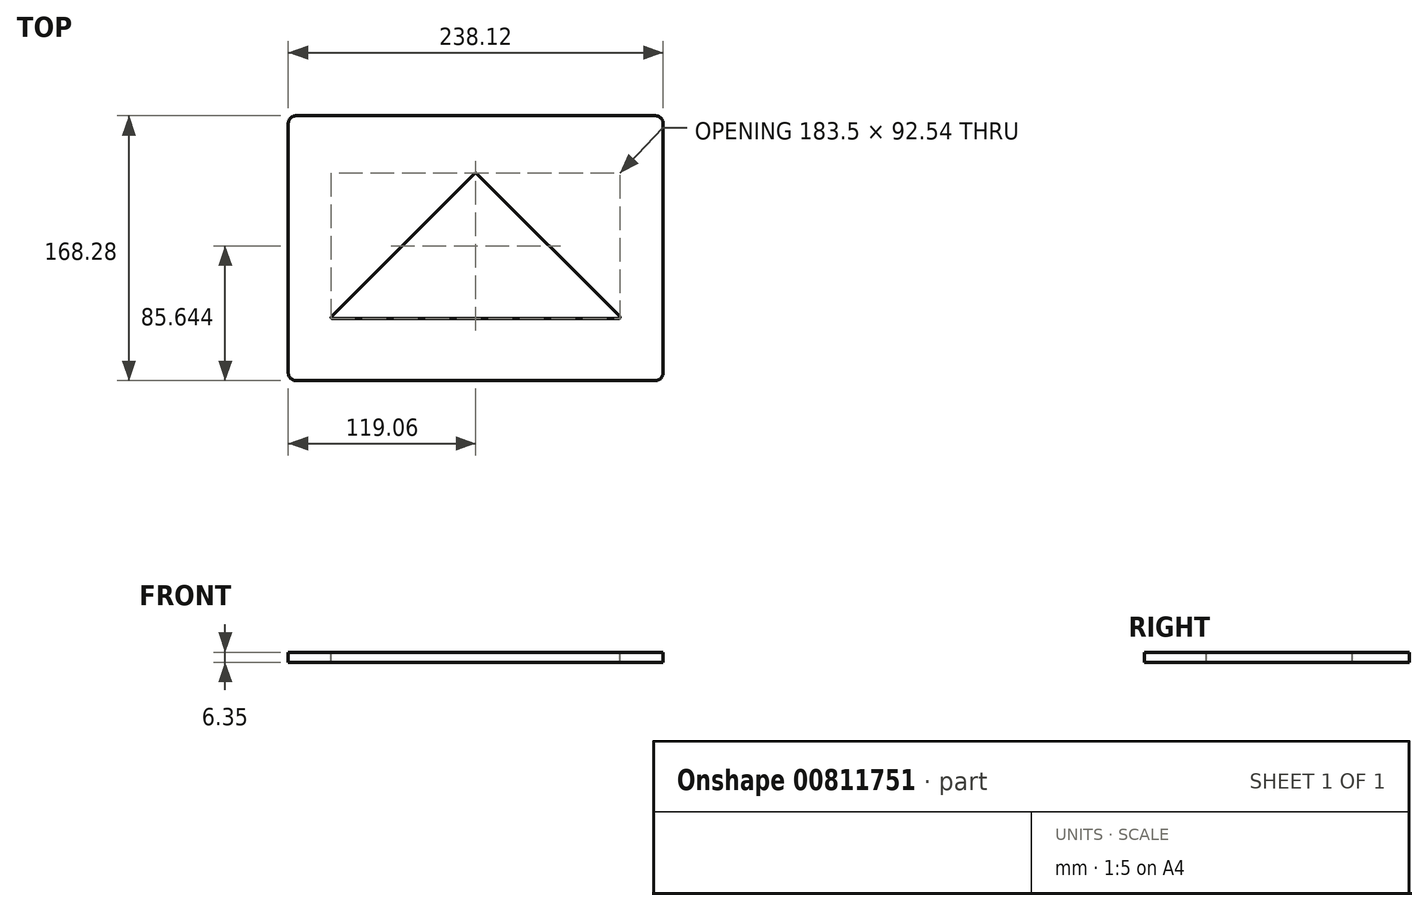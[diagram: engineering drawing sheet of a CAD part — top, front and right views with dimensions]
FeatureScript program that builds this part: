
annotation { "Feature Type Name" : "Feature", "Feature Type Description" : "" }
export const myFeature = defineFeature(function(context is Context, id is Id, definition is map)
    precondition{}
    {
        {
            var Q0;
            Q0=qCreatedBy(makeId("Top.planeOp"),FACE);
            var sketch = newSketch(context, id + "F0", { "sketchPlane" : qUnion([Q0])});
            skLineSegment(sketch, "E0.bottom", {"start": v(-113.98, 84.14) * mm, "end": v(113.98, 84.14) * mm});
            skLineSegment(sketch, "E0.top", {"start": v(-113.98, -84.14) * mm, "end": v(113.98, -84.14) * mm});
            skLineSegment(sketch, "E0.left", {"start": v(-119.06, 79.06) * mm, "end": v(-119.06, -79.06) * mm});
            skLineSegment(sketch, "E0.right", {"start": v(119.06, 79.06) * mm, "end": v(119.06, -79.06) * mm});
            skPoint(sketch, "E0.middle", {"position": v(0, 0) * mm});
            skPoint(sketch, "E1.visualSharp", {"position": v(-119.06, 84.14) * mm});
            skArc(sketch, "E1.filletArc", {"start": v(-113.98, 84.14) * mm, "mid": v(-117.57, 82.65) * mm, "end": v(-119.06, 79.06) * mm});
            skPoint(sketch, "E2.visualSharp", {"position": v(119.06, 84.14) * mm});
            skArc(sketch, "E2.filletArc", {"start": v(119.06, 79.06) * mm, "mid": v(117.57, 82.65) * mm, "end": v(113.98, 84.14) * mm});
            skPoint(sketch, "E3.visualSharp", {"position": v(119.06, -84.14) * mm});
            skArc(sketch, "E3.filletArc", {"start": v(113.98, -84.14) * mm, "mid": v(117.57, -82.65) * mm, "end": v(119.06, -79.06) * mm});
            skPoint(sketch, "E4.visualSharp", {"position": v(-119.06, -84.14) * mm});
            skArc(sketch, "E4.filletArc", {"start": v(-119.06, -79.06) * mm, "mid": v(-117.57, -82.65) * mm, "end": v(-113.98, -84.14) * mm});
            skSolve(sketch);
        }
        {
            var Q0;
            Q0 = qSketchRegion(id + "F0", true);
            extrude(context, id + "F1", {"entities" : qUnion([Q0]), "depth" : 6.35 * mm, "offsetDistance" : 25.4 * mm});
        }
        {
            var Q0;
            Q0=makeQuery(id+"F1.opExtrude","CAP_FACE",FACE,{"disambiguationData":[OSD([sQuery(id+"F0.wireOp",EDGE,"E0.bottom"),sQuery(id+"F0.wireOp",EDGE,"E0.top"),sQuery(id+"F0.wireOp",EDGE,"E0.left"),sQuery(id+"F0.wireOp",EDGE,"E0.right"),sQuery(id+"F0.wireOp",EDGE,"E1.filletArc"),sQuery(id+"F0.wireOp",EDGE,"E2.filletArc"),sQuery(id+"F0.wireOp",EDGE,"E3.filletArc"),sQuery(id+"F0.wireOp",EDGE,"E4.filletArc")])],"isStart":false});
            var sketch = newSketch(context, id + "F2", { "sketchPlane" : qUnion([Q0])});
            skLineSegment(sketch, "E5", {"start": v(-89.8, -43.5) * mm, "end": v(89.8, -43.5) * mm});
            skLineSegment(sketch, "E6", {"start": v(89.8, -43.5) * mm, "end": v(0, 46.3) * mm});
            skLineSegment(sketch, "E7", {"start": v(0, 46.3) * mm, "end": v(-89.8, -43.5) * mm});
            skSolve(sketch);
        }
        {
            var Q0;
            Q0 = qSketchRegion(id + "F2", true);
            extrude(context, id + "F3", {"entities" : qUnion([Q0]), "operationType" : NewBodyOperationType.REMOVE, "endBound" : BoundingType.THROUGH_ALL, "oppositeDirection" : true, "depth" : 25.4 * mm, "offsetDistance" : 25.4 * mm});
        }
        {
            var Q0;
            Q0=makeQuery(id+"F1.opExtrude","CAP_FACE",FACE,{"disambiguationData":[OSD([sQuery(id+"F0.wireOp",EDGE,"E0.bottom"),sQuery(id+"F0.wireOp",EDGE,"E0.top"),sQuery(id+"F0.wireOp",EDGE,"E0.left"),sQuery(id+"F0.wireOp",EDGE,"E0.right"),sQuery(id+"F0.wireOp",EDGE,"E1.filletArc"),sQuery(id+"F0.wireOp",EDGE,"E2.filletArc"),sQuery(id+"F0.wireOp",EDGE,"E3.filletArc"),sQuery(id+"F0.wireOp",EDGE,"E4.filletArc")])],"isStart":false});
            var sketch = newSketch(context, id + "F4", { "sketchPlane" : qUnion([Q0])});
            skLineSegment(sketch, "E8.0", {"start": v(-0.56, 47.54) * mm, "end": v(-91.52, -43.42) * mm});
            skLineSegment(sketch, "E8.1", {"start": v(91.52, -43.42) * mm, "end": v(0.56, 47.54) * mm});
            skLineSegment(sketch, "E8.2", {"start": v(-90.97, -44.77) * mm, "end": v(90.97, -44.77) * mm});
            skPoint(sketch, "E9.visualSharp", {"position": v(0, 48.1) * mm});
            skArc(sketch, "E9.filletArc", {"start": v(0.56, 47.54) * mm, "mid": v(0, 47.77) * mm, "end": v(-0.56, 47.54) * mm});
            skPoint(sketch, "E10.visualSharp", {"position": v(92.87, -44.77) * mm});
            skArc(sketch, "E10.filletArc", {"start": v(90.97, -44.77) * mm, "mid": v(91.7, -44.28) * mm, "end": v(91.52, -43.42) * mm});
            skPoint(sketch, "E11.visualSharp", {"position": v(-92.87, -44.77) * mm});
            skArc(sketch, "E11.filletArc", {"start": v(-91.52, -43.42) * mm, "mid": v(-91.7, -44.28) * mm, "end": v(-90.97, -44.77) * mm});
            skSolve(sketch);
        }
        {
            var Q0;
            Q0 = qSketchRegion(id + "F4", true);
            extrude(context, id + "F5", {"entities" : qUnion([Q0]), "operationType" : NewBodyOperationType.REMOVE, "endBound" : BoundingType.THROUGH_ALL, "oppositeDirection" : true, "depth" : 25.4 * mm, "offsetDistance" : 25.4 * mm});
        }
    });
